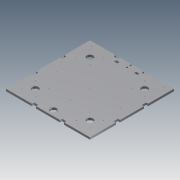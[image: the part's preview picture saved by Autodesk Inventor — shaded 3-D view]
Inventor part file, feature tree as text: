
AUTODESK INVENTOR PART (.ipt)
format: ipt  version: 2011 (Build 150239000, 239)  size: 1,369,600 bytes
history: native  units: in
note: dims shown in document units (in); Inventor stores cm internally (conversion verified against a paired STEP export)
features: sketch x45, extrude x44
ambient origin geometry x8: Origin, YZ Plane, XZ Plane, XY Plane, X Axis, Y Axis, Z Axis, Center Point
bodies: Solid1 (feature_tree)
feature tree (89):
  sketch  "Sketch1"  dims[d0=20.0in d1=20.0in]
  extrude  "Extrusion1"  Depth=20.0in
  extrude  "Extrusion2"  Depth=3.5in
  extrude  "Extrusion3"  Depth=3.5in
  extrude  "Extrusion4"  Depth=3.5in
  extrude  "Extrusion5"  Depth=3.5in
  extrude  "Extrusion6"  Depth=1.911in
  extrude  "Extrusion7"  Depth=5.089in
  extrude  "Extrusion8"  Depth=5.089in
  extrude  "Extrusion9"  Depth=1.911in
  extrude  "Extrusion10"  Depth=0.156in
  extrude  "Extrusion11"  Depth=0.156in
  extrude  "Extrusion12"  Depth=0.156in
  extrude  "Extrusion13"  Depth=0.156in
  extrude  "Extrusion14"  Depth=0.156in
  extrude  "Extrusion15"  Depth=0.156in
  extrude  "Extrusion16"  Depth=0.156in
  extrude  "Extrusion17"  Depth=0.156in
  extrude  "Extrusion18"  Depth=1.0in
  extrude  "Extrusion19"  Depth=1.0in
  extrude  "Extrusion20"  Depth=0.5in TaperAngle=0.0deg
  extrude  "Extrusion21"  Depth=0.5in
  extrude  "Extrusion22"  Depth=1.5in
  extrude  "Extrusion23"  Depth=1.5in
  extrude  "Extrusion24"  Depth=1.5in
  extrude  "Extrusion25"  Depth=1.5in
  extrude  "Extrusion26"  Depth=1.5in
  extrude  "Extrusion27"  Depth=1.5in
  extrude  "Extrusion28"  Depth=1.5in
  extrude  "Extrusion29"  Depth=1.0in TaperAngle=0.0deg
  extrude  "Extrusion30"  Depth=0.5in TaperAngle=0.0deg
  extrude  "Extrusion31"  Depth=0.25in TaperAngle=0.0deg
  extrude  "Extrusion32"  Depth=2.6in
  extrude  "Extrusion33"  Depth=7.4in
  extrude  "Extrusion34"  Depth=0.25in
  extrude  "Extrusion35"  Depth=0.25in
  extrude  "Extrusion36"  Depth=0.25in
  extrude  "Extrusion37"  Depth=0.25in
  extrude  "Extrusion38"  Depth=0.25in
  extrude  "Extrusion39"  Depth=0.25in
  extrude  "Extrusion40"  Depth=0.25in TaperAngle=0.0deg
  extrude  "Extrusion41"  Depth=1.5in
  extrude  "Extrusion42"  Depth=1.5in
  extrude  "Extrusion43"  Depth=0.25in
  extrude  "Extrusion44"  Depth=0.25in
  sketch  "Sketch2"  dims[d2=3.5in d3=3.5in]
  sketch  "Sketch3"  dims[d4=3.5in d5=3.5in]
  sketch  "Sketch4"  dims[d6=3.5in d7=3.5in]
  sketch  "Sketch5"  dims[d8=3.5in d9=3.5in]
  sketch  "Sketch6"  dims[d10=1.911in d11=1.911in]
  sketch  "Sketch7"  dims[d12=1.911in d13=5.089in]
  sketch  "Sketch8"  dims[d14=5.089in d15=5.089in]
  sketch  "Sketch9"  dims[d16=5.089in d17=1.911in]
  sketch  "Sketch10"  dims[d18=1.911in d19=0.156in]
  sketch  "Sketch11"  dims[d20=0.156in d21=0.156in]
  sketch  "Sketch12"  dims[d22=0.156in d23=0.156in]
  sketch  "Sketch13"  dims[d24=0.156in d25=0.156in]
  sketch  "Sketch14"  dims[d26=0.156in d27=0.156in]
  sketch  "Sketch15"  dims[d28=0.156in d29=0.156in]
  sketch  "Sketch16"  dims[d30=0.156in d31=0.156in]
  sketch  "Sketch17"  dims[d32=0.156in d33=0.156in]
  sketch  "Sketch18"  dims[d34=0.156in d35=1.0in]
  sketch  "Sketch19"  dims[d36=1.0in d37=1.0in]
  sketch  "Sketch20"  dims[d38=1.0in d39=0.5in d40=0.0in]
  sketch  "Sketch21"  dims[d41=0.5in d42=0.5in]
  sketch  "Sketch22"  dims[d43=1.0in d44=1.5in]
  sketch  "Sketch23"  dims[d45=1.0in d46=1.5in]
  sketch  "Sketch24"  dims[d47=1.0in d48=1.5in]
  sketch  "Sketch25"  dims[d49=1.0in d50=1.5in]
  sketch  "Sketch26"  dims[d51=1.0in d52=1.5in]
  sketch  "Sketch27"  dims[d53=1.0in d54=1.5in]
  sketch  "Sketch28"  dims[d55=1.0in d56=1.5in]
  sketch  "Sketch29"  dims[d57=1.0in d58=1.0in d59=0.0in]
  sketch  "Sketch30"  dims[d60=1.0in d61=0.0in d62=0.5in d63=0.0in]
  sketch  "Sketch31"  dims[d64=0.5in d65=0.0in d66=0.25in d67=0.0in]
  sketch  "Sketch32"  dims[d68=10.0in d69=2.6in]
  sketch  "Sketch33"  dims[d70=5.2in d71=7.4in]
  sketch  "Sketch34"  dims[d72=5.2in d73=0.25in]
  sketch  "Sketch35"  dims[d74=0.25in d75=0.25in]
  sketch  "Sketch36"  dims[d76=0.25in d77=0.25in]
  sketch  "Sketch37"  dims[d78=0.25in d79=0.25in]
  sketch  "Sketch38"  dims[d80=0.25in d81=0.25in]
  sketch  "Sketch39"  dims[d82=0.25in d83=0.25in]
  sketch  "Sketch40"  dims[d84=0.25in d85=0.25in d86=0.0in]
  sketch  "Sketch41"  dims[d87=1.5in d88=1.5in]
  sketch  "Sketch42"  dims[d89=1.5in d90=1.5in]
  sketch  "Sketch43"  dims[d91=0.25in d92=0.25in]
  sketch  "Sketch44"  dims[d93=0.25in d94=0.25in]
  sketch  "Sketch45"  dims[d95=0.25in d96=0.25in d97=0.25in d98=0.25in d99=0.25in d100=0.25in d101=0.25in d102=0.25in d103=0.0in d104=1.0in d105=1.0in d106=1.0in d107=1.0in d108=1.0in d109=1.0in d110=1.0in d111=1.0in d112=1.0in d113=1.0in d114=1.0in d115=1.0in d116=1.0in d117=1.0in d118=1.0in d119=1.0in d120=1.0in d121=1.0in d122=1.0in d123=1.0in d124=0.25in d125=1.0in d126=0.0in d127=1.0in d128=0.0in d129=1.5in d130=1.0in d131=0.0in d132=0.25in d133=0.25in d134=0.25in d135=0.25in d136=0.25in d137=0.25in d138=0.25in d139=0.25in d140=0.25in d141=0.25in d142=0.25in d143=0.25in d144=0.25in d145=0.0in d146=0.25in d147=0.0in d148=0.25in d149=1.5in d150=1.25in d151=1.0in d152=2.0in d153=1.0in d154=2.0in d155=1.0in d156=2.0in d157=1.0in d158=0.345in d159=0.25in d160=0.0in d161=0.25in d162=0.0in d163=2.25in d164=0.25in d165=1.0in d166=3.0in d167=1.0in d168=3.0in d169=1.0in d170=3.0in d171=1.0in d172=3.0in d173=1.0in d174=0.25in d175=0.0in d176=0.25in d177=0.25in d178=0.25in d179=0.0in d180=0.25in d181=0.25in d182=0.5in d183=0.5in d184=0.25in d185=0.0in d186=0.25in d187=0.0in d188=0.25in d189=0.0in d190=0.25in d191=0.0in d192=1.0in d193=1.0in d194=0.25in d195=3.25in d196=1.0in d197=3.0in d198=1.0in d199=3.0in d200=1.0in d201=3.25in d202=1.0in d203=0.5in d204=0.5in d205=0.5in d206=0.5in d207=0.25in d208=0.0in d209=0.25in d210=0.0in d211=1.594in d212=1.594in d213=3.188in d214=3.188in d215=1.594in d216=1.594in d217=3.188in d218=3.188in d219=0.156in d220=0.156in d221=0.156in d222=0.156in d223=0.156in d224=0.156in d225=0.156in d226=0.156in d227=0.156in d228=0.156in d229=0.156in d230=0.156in d231=0.156in d232=0.156in d233=0.156in d234=0.156in d235=0.25in d236=0.0in d237=0.25in d238=0.0in d239=0.25in d240=0.0in d241=0.25in d242=0.0in d243=6.65in d244=6.7in d245=0.5in d246=0.5in d247=0.0in d248=0.5in d249=0.5in d250=0.5in d251=0.5in d252=0.0in d253=0.25in d254=0.25in d255=0.5in d256=0.0in d257=0.25in d258=0.5in d259=0.0in d260=0.25in d261=0.5in d262=0.0in d263=0.25in d264=0.25in d265=0.5in d266=0.0in d267=3.85in d268=7.7in d269=0.5in d270=1.0in d271=1.0in d272=0.5in d273=0.5in d274=1.0in d275=0.0in d276=9.0in d277=7.7in d278=0.5in d279=1.0in d280=9.0in d281=0.5in d282=1.0in d283=0.0in d284=1.5in d285=1.0in d286=0.156in d287=1.5in d288=1.0in d289=0.156in d290=1.0in d291=0.0in d292=10.35in d293=1.0in d294=1.0in d295=1.0in d296=1.0in d297=0.156in d298=0.156in d299=1.0in d300=0.0in d301=0.315in d302=0.3937in d303=1.1811in d304=1.0in d305=0.0in d306=4.3307in d307=0.8465in d308=1.6929in d309=0.1969in d310=1.25in d311=0.0984in d312=0.156in d313=0.156in d314=1.0in d315=0.0in d316=0.5in d317=0.0in d318=1.5in d319=2.0in d320=4.0in d321=0.75in d322=0.5in d323=0.75in d324=0.5in d325=0.5in d326=0.0in d327=0.5in d328=0.0in d329=9.25in d330=2.43in d331=4.54in d332=0.156in d333=0.156in d334=0.5in d335=0.0in d336=1.15in d337=1.3in d338=0.25in d339=1.3in d340=0.1969in d341=0.8543in d342=1.7087in d343=0.15in d344=0.5in d345=0.0in]
